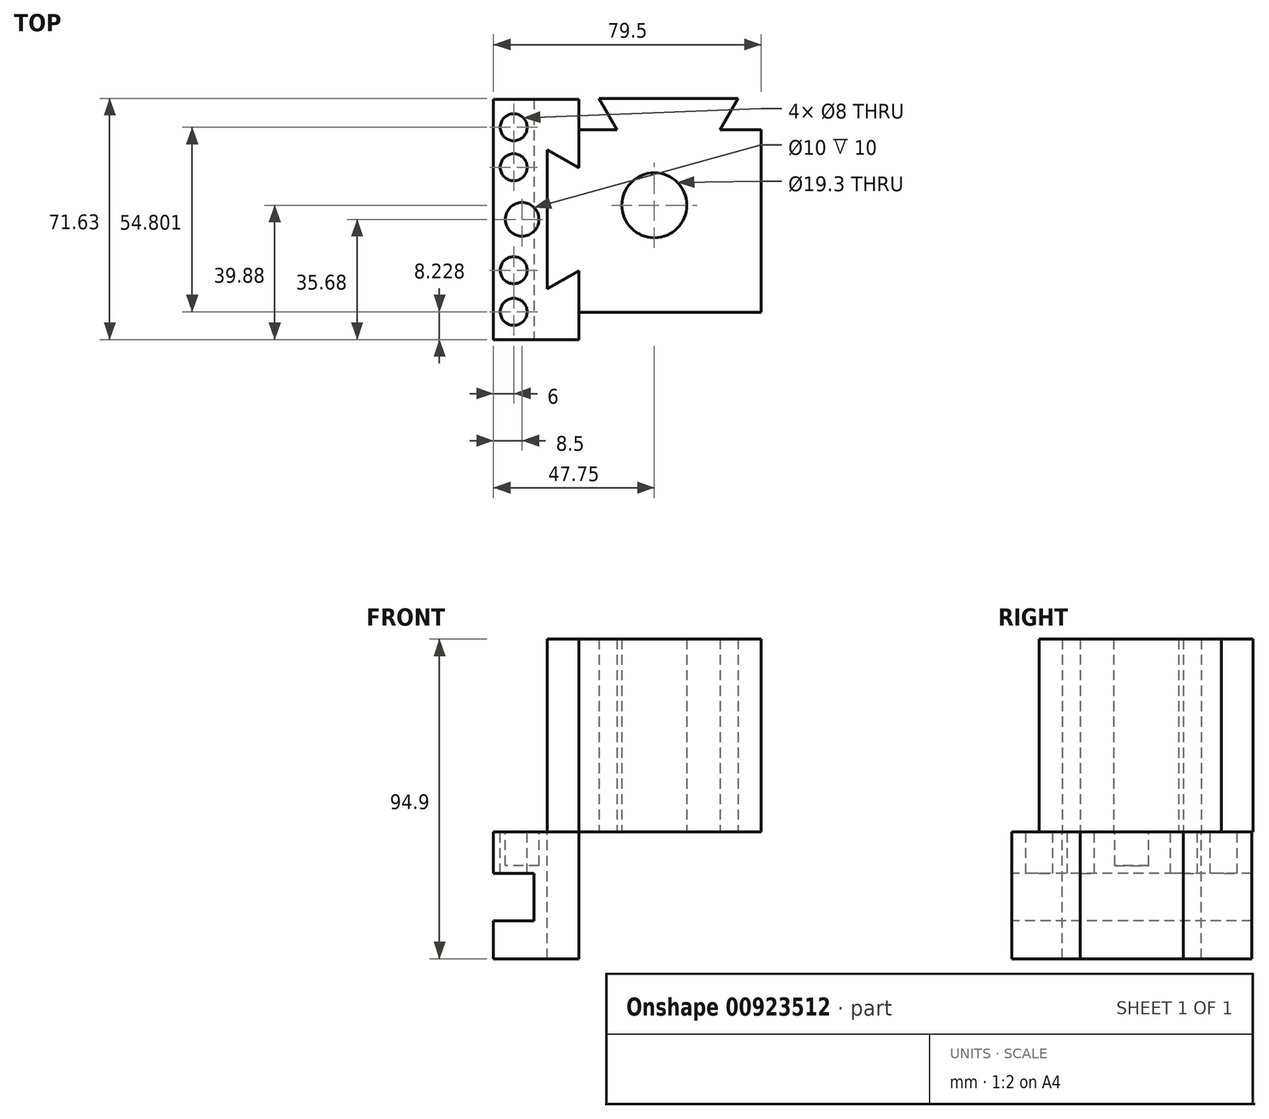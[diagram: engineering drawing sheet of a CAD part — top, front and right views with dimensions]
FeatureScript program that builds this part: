
annotation { "Feature Type Name" : "Feature", "Feature Type Description" : "" }
export const myFeature = defineFeature(function(context is Context, id is Id, definition is map)
    precondition{}
    {
        {
            var Q0;
            Q0=qCreatedBy(makeId("Top.planeOp"),FACE);
            var sketch = newSketch(context, id + "F0", { "sketchPlane" : qUnion([Q0])});
            skLineSegment(sketch, "E0.bottom", {"start": v(31.75, -31.75) * mm, "end": v(-22.45, -31.75) * mm});
            skLineSegment(sketch, "E0.top", {"start": v(31.75, 31.75) * mm, "end": v(24.85, 31.75) * mm, "construction": true});
            skLineSegment(sketch, "E0.left", {"start": v(31.75, -31.75) * mm, "end": v(31.75, 22.45) * mm});
            skLineSegment(sketch, "E0.right", {"start": v(-31.75, -31.75) * mm, "end": v(-31.75, -24.85) * mm, "construction": true});
            skPoint(sketch, "E0.middle", {"position": v(0, 0) * mm});
            skLineSegment(sketch, "E1", {"start": v(-31.75, 22.45) * mm, "end": v(-22.45, 22.45) * mm, "construction": true});
            skLineSegment(sketch, "E2", {"start": v(-16.45, 31.75) * mm, "end": v(-11.08, 22.45) * mm});
            skLineSegment(sketch, "E3", {"start": v(19.48, 22.45) * mm, "end": v(24.85, 31.75) * mm});
            skLineSegment(sketch, "E4", {"start": v(-22.45, -31.75) * mm, "end": v(-22.45, -19.48) * mm});
            skCircle(sketch, "E5", {"center": v(0, 0) * mm, "radius": 9.65 * mm});
            skLineSegment(sketch, "E6", {"start": v(-31.75, -24.85) * mm, "end": v(-22.45, -19.48) * mm});
            skLineSegment(sketch, "E7", {"start": v(-22.45, 11.08) * mm, "end": v(-31.75, 16.45) * mm});
            skLineSegment(sketch, "E8", {"start": v(31.75, 22.45) * mm, "end": v(31.75, 22.45) * mm});
            skLineSegment(sketch, "E9", {"start": v(-22.45, 22.45) * mm, "end": v(-22.45, 31.75) * mm, "construction": true});
            skLineSegment(sketch, "E10", {"start": v(-22.45, 22.45) * mm, "end": v(-11.08, 22.45) * mm});
            skLineSegment(sketch, "E11", {"start": v(-11.08, 22.45) * mm, "end": v(-11.08, 22.45) * mm});
            skLineSegment(sketch, "E12", {"start": v(-11.08, 22.45) * mm, "end": v(19.48, 22.45) * mm, "construction": true});
            skLineSegment(sketch, "E13", {"start": v(19.48, 22.45) * mm, "end": v(31.75, 22.45) * mm});
            skLineSegment(sketch, "E14", {"start": v(-22.45, 11.08) * mm, "end": v(-22.45, 22.45) * mm});
            skLineSegment(sketch, "E15", {"start": v(-22.45, -19.48) * mm, "end": v(-22.45, 11.08) * mm, "construction": true});
            skLineSegment(sketch, "E16", {"start": v(-31.75, 16.45) * mm, "end": v(-31.75, 31.75) * mm, "construction": true});
            skLineSegment(sketch, "E17", {"start": v(-22.45, 31.75) * mm, "end": v(-31.75, 31.75) * mm, "construction": true});
            skLineSegment(sketch, "E18", {"start": v(24.85, 31.75) * mm, "end": v(-16.45, 31.75) * mm});
            skLineSegment(sketch, "E19", {"start": v(31.75, 22.45) * mm, "end": v(31.75, 31.75) * mm, "construction": true});
            skLineSegment(sketch, "E20", {"start": v(-31.75, -24.85) * mm, "end": v(-31.75, 16.45) * mm});
            skLineSegment(sketch, "E21", {"start": v(-22.45, -31.75) * mm, "end": v(-31.75, -31.75) * mm, "construction": true});
            skLineSegment(sketch, "E22", {"start": v(-16.45, 31.75) * mm, "end": v(-22.45, 31.75) * mm, "construction": true});
            skSolve(sketch);
        }
        {
            var Q0;
            Q0=makeQuery(id+"F0.imprint","IMPRINT",FACE,{"disambiguationData":[TD([[makeQuery(id+"F0.imprint","IMPRINT",EDGE,{"derivedFrom":sQuery(id+"F0.wireOp",EDGE,"E0.bottom")}),-1.0]])]});
            extrude(context, id + "F1", {"entities" : qUnion([Q0]), "depth" : 57.2 * mm, "offsetDistance" : 25 * mm});
        }
        {
            var Q0;
            Q0=qCreatedBy(makeId("Top.planeOp"),FACE);
            var sketch = newSketch(context, id + "F2", { "sketchPlane" : qUnion([Q0])});
            skPoint(sketch, "E23.0", {"position": v(-22.45, 11.08) * mm});
            skLineSegment(sketch, "E24.0", {"start": v(-22.45, 11.08) * mm, "end": v(-31.75, 16.45) * mm});
            skLineSegment(sketch, "E25.0", {"start": v(-31.75, -24.85) * mm, "end": v(-31.75, 16.45) * mm});
            skLineSegment(sketch, "E26.0", {"start": v(-31.75, -24.85) * mm, "end": v(-22.45, -19.48) * mm});
            skLineSegment(sketch, "E27.0", {"start": v(-22.45, -31.75) * mm, "end": v(-22.45, -19.48) * mm});
            skLineSegment(sketch, "E28.0", {"start": v(-22.45, 11.08) * mm, "end": v(-22.45, 22.45) * mm});
            skLineSegment(sketch, "E29", {"start": v(-22.45, 22.45) * mm, "end": v(-22.45, 31.48) * mm});
            skLineSegment(sketch, "E30", {"start": v(-22.45, 31.48) * mm, "end": v(-47.75, 31.48) * mm});
            skLineSegment(sketch, "E31", {"start": v(-47.75, 31.48) * mm, "end": v(-47.75, -39.88) * mm});
            skLineSegment(sketch, "E32", {"start": v(-47.75, -39.88) * mm, "end": v(-22.45, -39.88) * mm});
            skLineSegment(sketch, "E33", {"start": v(-22.45, -39.88) * mm, "end": v(-22.45, -31.75) * mm});
            skLineSegment(sketch, "E34", {"start": v(-41.75, 31.48) * mm, "end": v(-41.75, -39.88) * mm, "construction": true});
            skLineSegment(sketch, "E35", {"start": v(-39.25, 31.48) * mm, "end": v(-39.25, -39.88) * mm, "construction": true});
            skCircle(sketch, "E36", {"center": v(-39.25, -4.2) * mm, "radius": 5 * mm});
            skCircle(sketch, "E37", {"center": v(-41.75, 23.15) * mm, "radius": 4 * mm});
            skCircle(sketch, "E38", {"center": v(-41.75, 11.27) * mm, "radius": 4 * mm});
            skCircle(sketch, "E39", {"center": v(-41.75, -19.3) * mm, "radius": 4 * mm});
            skCircle(sketch, "E40", {"center": v(-41.75, -31.65) * mm, "radius": 4 * mm});
            skSolve(sketch);
        }
        {
            var Q0;
            Q0=makeQuery(id+"F2.imprint","IMPRINT",FACE,{"disambiguationData":[TD([[makeQuery(id+"F2.imprint","IMPRINT",EDGE,{"derivedFrom":sQuery(id+"F2.wireOp",EDGE,"E24.0")}),-1.0]])]});
            var Q1;
            Q1=makeQuery(id+"F2.imprint","IMPRINT",FACE,{"disambiguationData":[TD([[makeQuery(id+"F2.imprint","IMPRINT",EDGE,{"derivedFrom":sQuery(id+"F2.wireOp",EDGE,"E40")}),1.0]])]});
            var Q2;
            Q2=makeQuery(id+"F2.imprint","IMPRINT",FACE,{"disambiguationData":[TD([[makeQuery(id+"F2.imprint","IMPRINT",EDGE,{"derivedFrom":sQuery(id+"F2.wireOp",EDGE,"E39")}),1.0]])]});
            var Q3;
            Q3=makeQuery(id+"F2.imprint","IMPRINT",FACE,{"disambiguationData":[TD([[makeQuery(id+"F2.imprint","IMPRINT",EDGE,{"derivedFrom":sQuery(id+"F2.wireOp",EDGE,"E36")}),1.0]])]});
            var Q4;
            Q4=makeQuery(id+"F2.imprint","IMPRINT",FACE,{"disambiguationData":[TD([[makeQuery(id+"F2.imprint","IMPRINT",EDGE,{"derivedFrom":sQuery(id+"F2.wireOp",EDGE,"E38")}),1.0]])]});
            var Q5;
            Q5=makeQuery(id+"F2.imprint","IMPRINT",FACE,{"disambiguationData":[TD([[makeQuery(id+"F2.imprint","IMPRINT",EDGE,{"derivedFrom":sQuery(id+"F2.wireOp",EDGE,"E37")}),1.0]])]});
            extrude(context, id + "F3", {"entities" : qUnion([Q0, Q1, Q2, Q3, Q4, Q5]), "oppositeDirection" : true, "depth" : 37.7 * mm, "offsetDistance" : 25 * mm});
        }
        {
            var Q0;
            Q0=makeQuery(id+"F3.opExtrude","SWEPT_FACE",FACE,{"disambiguationData":[OSD([sQuery(id+"F2.wireOp",EDGE,"E32")])]});
            var sketch = newSketch(context, id + "F4", { "sketchPlane" : qUnion([Q0])});
            skLineSegment(sketch, "E41", {"start": v(-47.75, -12.4) * mm, "end": v(-35.75, -12.4) * mm});
            skLineSegment(sketch, "E42", {"start": v(-35.75, -12.4) * mm, "end": v(-35.75, -26.5) * mm});
            skLineSegment(sketch, "E43", {"start": v(-35.75, -26.5) * mm, "end": v(-47.75, -26.5) * mm});
            skLineSegment(sketch, "E44", {"start": v(-47.75, -26.5) * mm, "end": v(-47.75, -12.4) * mm});
            skSolve(sketch);
        }
        {
            var Q0;
            Q0=makeQuery(id+"F4.imprint","IMPRINT",FACE,{"disambiguationData":[TD([[makeQuery(id+"F4.imprint","IMPRINT",EDGE,{"derivedFrom":sQuery(id+"F4.wireOp",EDGE,"E41")}),-1.0]])]});
            extrude(context, id + "F5", {"entities" : qUnion([Q0]), "operationType" : NewBodyOperationType.REMOVE, "endBound" : BoundingType.THROUGH_ALL, "oppositeDirection" : true, "depth" : 25 * mm, "offsetDistance" : 25 * mm});
        }
        {
            var Q0;
            Q0=makeQuery(id+"F2.imprint","IMPRINT",FACE,{"disambiguationData":[TD([[makeQuery(id+"F2.imprint","IMPRINT",EDGE,{"derivedFrom":sQuery(id+"F2.wireOp",EDGE,"E36")}),1.0]])]});
            var Q1;
            Q1=sQuery(id+"F2.wireOp",EDGE,"E36");
            extrude(context, id + "F6", {"entities" : qUnion([Q0]), "operationType" : NewBodyOperationType.REMOVE, "surfaceEntities" : qUnion([Q1]), "oppositeDirection" : true, "depth" : 10 * mm, "offsetDistance" : 25 * mm});
        }
        {
            var Q0;
            Q0=makeQuery(id+"F2.imprint","IMPRINT",FACE,{"disambiguationData":[TD([[makeQuery(id+"F2.imprint","IMPRINT",EDGE,{"derivedFrom":sQuery(id+"F2.wireOp",EDGE,"E37")}),1.0]])]});
            var Q1;
            Q1=makeQuery(id+"F2.imprint","IMPRINT",FACE,{"disambiguationData":[TD([[makeQuery(id+"F2.imprint","IMPRINT",EDGE,{"derivedFrom":sQuery(id+"F2.wireOp",EDGE,"E38")}),1.0]])]});
            var Q2;
            Q2=makeQuery(id+"F2.imprint","IMPRINT",FACE,{"disambiguationData":[TD([[makeQuery(id+"F2.imprint","IMPRINT",EDGE,{"derivedFrom":sQuery(id+"F2.wireOp",EDGE,"E39")}),1.0]])]});
            var Q3;
            Q3=makeQuery(id+"F2.imprint","IMPRINT",FACE,{"disambiguationData":[TD([[makeQuery(id+"F2.imprint","IMPRINT",EDGE,{"derivedFrom":sQuery(id+"F2.wireOp",EDGE,"E40")}),1.0]])]});
            var Q4;
            Q4=sQuery(id+"F2.wireOp",EDGE,"E37");
            var Q5;
            Q5=sQuery(id+"F2.wireOp",EDGE,"E38");
            var Q6;
            Q6=sQuery(id+"F2.wireOp",EDGE,"E39");
            var Q7;
            Q7=sQuery(id+"F2.wireOp",EDGE,"E40");
            var Q8;
            Q8=makeQuery(id+"F5.boolean.opBoolean","COPY",FACE,{"derivedFrom":makeQuery(id+"F5.opExtrude","SWEPT_FACE",FACE,{"disambiguationData":[OSD([sQuery(id+"F4.wireOp",EDGE,"E41")])]})});
            extrude(context, id + "F7", {"entities" : qUnion([Q0, Q1, Q2, Q3]), "operationType" : NewBodyOperationType.REMOVE, "surfaceEntities" : qUnion([Q4, Q5, Q6, Q7]), "endBound" : BoundingType.UP_TO_SURFACE, "oppositeDirection" : true, "depth" : 25 * mm, "endBoundEntityFace" : qUnion([Q8]), "offsetDistance" : 25 * mm});
        }
    });
